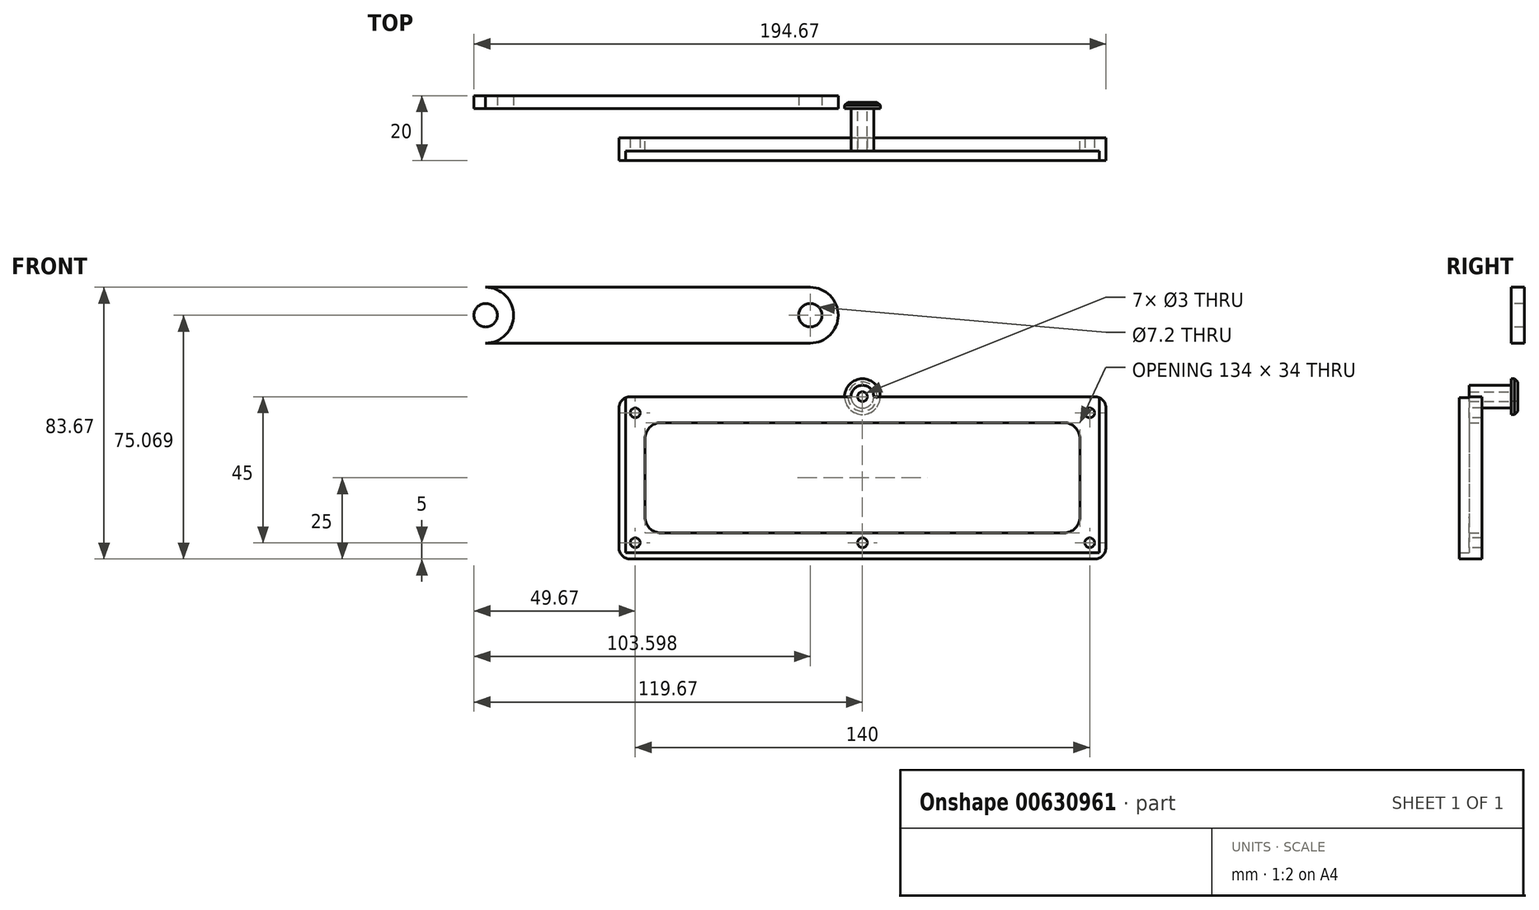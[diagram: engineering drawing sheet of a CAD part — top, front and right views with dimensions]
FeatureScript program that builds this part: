
annotation { "Feature Type Name" : "Feature", "Feature Type Description" : "" }
export const myFeature = defineFeature(function(context is Context, id is Id, definition is map)
    precondition{}
    {
        {
            var Q0;
            Q0=qCreatedBy(makeId("Front.planeOp"),FACE);
            var sketch = newSketch(context, id + "F0", { "sketchPlane" : qUnion([Q0])});
            skLineSegment(sketch, "E0.bottom", {"start": v(75, 25) * mm, "end": v(-75, 25) * mm});
            skLineSegment(sketch, "E0.top", {"start": v(75, -25) * mm, "end": v(-75, -25) * mm});
            skLineSegment(sketch, "E0.left", {"start": v(75, 25) * mm, "end": v(75, -25) * mm});
            skLineSegment(sketch, "E0.right", {"start": v(-75, 25) * mm, "end": v(-75, -25) * mm});
            skPoint(sketch, "E0.middle", {"position": v(0, 0) * mm});
            skLineSegment(sketch, "E1.bottom", {"start": v(-67, 17) * mm, "end": v(67, 17) * mm});
            skLineSegment(sketch, "E1.top", {"start": v(-67, -17) * mm, "end": v(67, -17) * mm});
            skLineSegment(sketch, "E1.left", {"start": v(-67, 17) * mm, "end": v(-67, -17) * mm});
            skLineSegment(sketch, "E1.right", {"start": v(67, 17) * mm, "end": v(67, -17) * mm});
            skLineSegment(sketch, "E2", {"start": v(0, 17) * mm, "end": v(0, 25) * mm, "construction": true});
            skArc(sketch, "E3", {"start": v(-6.5, 25) * mm, "mid": v(0, 31.5) * mm, "end": v(6.5, 25) * mm});
            skCircle(sketch, "E4", {"center": v(0, 25) * mm, "radius": 1.5 * mm});
            skLineSegment(sketch, "E5.bottom", {"start": v(7.5, 17) * mm, "end": v(-7.5, 17) * mm});
            skLineSegment(sketch, "E5.top", {"start": v(7.5, -17) * mm, "end": v(-7.5, -17) * mm});
            skLineSegment(sketch, "E5.left", {"start": v(7.5, 17) * mm, "end": v(7.5, -17) * mm});
            skLineSegment(sketch, "E5.right", {"start": v(-7.5, 17) * mm, "end": v(-7.5, -17) * mm});
            skCircle(sketch, "E6", {"center": v(0, 25) * mm, "radius": 3.5 * mm});
            skSolve(sketch);
        }
        {
            var Q0;
            Q0=makeQuery(id+"F0.imprint","IMPRINT",FACE,{"disambiguationData":[TD([[makeQuery(id+"F0.imprint","IMPRINT",EDGE,{"derivedFrom":sQuery(id+"F0.wireOp",EDGE,"E0.top")}),-1.0]])]});
            var Q1;
            {var subQ0=sQuery(id+"F0.wireOp",EDGE,"E3");Q1=makeQuery(id+"F0.imprint","IMPRINT",FACE,{"disambiguationData":[TD([[makeQuery(id+"F0.imprint","IMPRINT",EDGE,{"derivedFrom":subQ0}),-1.0]])]});}
            var Q2;
            Q2=makeQuery(id+"F0.imprint","IMPRINT",FACE,{"disambiguationData":[TD([[makeQuery(id+"F0.imprint","IMPRINT",EDGE,{"derivedFrom":sQuery(id+"F0.wireOp",EDGE,"E5.bottom")}),1.0]])]});
            var Q3;
            {var subQ0=sQuery(id+"F0.wireOp",EDGE,"E6");var subQ1=sQuery(id+"F0.wireOp",EDGE,"E0.bottom");var subQ2=makeQuery(id+"F0.imprint","INTERSECT",VERTEX,{"disambiguationData":[OD(0.0)],"derivedFrom":[subQ1,subQ0]});Q3=makeQuery(id+"F0.imprint","IMPRINT",FACE,{"disambiguationData":[TD([[makeQuery(id+"F0.imprint","IMPRINT",EDGE,{"disambiguationData":[TD([[subQ2,-1.0]])],"derivedFrom":subQ1}),1.0]])]});}
            var Q4;
            {var subQ0=sQuery(id+"F0.wireOp",EDGE,"E6");var subQ1=sQuery(id+"F0.wireOp",EDGE,"E0.bottom");var subQ2=makeQuery(id+"F0.imprint","INTERSECT",VERTEX,{"disambiguationData":[OD(0.0)],"derivedFrom":[subQ1,subQ0]});Q4=makeQuery(id+"F0.imprint","IMPRINT",FACE,{"disambiguationData":[TD([[makeQuery(id+"F0.imprint","IMPRINT",EDGE,{"disambiguationData":[TD([[subQ2,-1.0]])],"derivedFrom":subQ1}),-1.0]])]});}
            extrude(context, id + "F1", {"entities" : qUnion([Q0, Q1, Q2, Q3, Q4]), "depth" : 4 * mm, "offsetDistance" : 25 * mm});
        }
        {
            var Q0;
            {var subQ0=sQuery(id+"F0.wireOp",EDGE,"E3");var subQ1=sQuery(id+"F0.wireOp",EDGE,"E0.bottom");Q0=makeQuery(id+"F1.opExtrude","SWEPT_EDGE",EDGE,{"disambiguationData":[OSD([subQ1,subQ0]),TDD([makeQuery(id+"F0.imprint","INTERSECT",VERTEX,{"disambiguationData":[OD(0.0)],"derivedFrom":[subQ1,subQ0]})])]});}
            var Q1;
            {var subQ0=sQuery(id+"F0.wireOp",EDGE,"E3");var subQ1=sQuery(id+"F0.wireOp",EDGE,"E0.bottom");Q1=makeQuery(id+"F1.opExtrude","SWEPT_EDGE",EDGE,{"disambiguationData":[OSD([subQ1,subQ0]),TDD([makeQuery(id+"F0.imprint","INTERSECT",VERTEX,{"disambiguationData":[OD(1.0)],"derivedFrom":[subQ1,subQ0]})])]});}
            var Q2;
            Q2=makeQuery(id+"F1.opExtrude","SWEPT_EDGE",EDGE,{"disambiguationData":[OSD([sQuery(id+"F0.wireOp",EDGE,"E1.bottom"),sQuery(id+"F0.wireOp",EDGE,"E5.bottom"),sQuery(id+"F0.wireOp",EDGE,"E5.right")])]});
            var Q3;
            Q3=makeQuery(id+"F1.opExtrude","SWEPT_EDGE",EDGE,{"disambiguationData":[OSD([sQuery(id+"F0.wireOp",EDGE,"E1.bottom"),sQuery(id+"F0.wireOp",EDGE,"E5.bottom"),sQuery(id+"F0.wireOp",EDGE,"E5.left")])]});
            var Q4;
            Q4=makeQuery(id+"F1.opExtrude","SWEPT_EDGE",EDGE,{"disambiguationData":[OSD([sQuery(id+"F0.wireOp",EDGE,"E1.top"),sQuery(id+"F0.wireOp",EDGE,"E5.top"),sQuery(id+"F0.wireOp",EDGE,"E5.left")])]});
            var Q5;
            Q5=makeQuery(id+"F1.opExtrude","SWEPT_EDGE",EDGE,{"disambiguationData":[OSD([sQuery(id+"F0.wireOp",EDGE,"E1.top"),sQuery(id+"F0.wireOp",EDGE,"E5.top"),sQuery(id+"F0.wireOp",EDGE,"E5.right")])]});
            fillet(context, id + "F2", {"entities" : qUnion([Q0, Q1, Q2, Q3, Q4, Q5]), "radius" : 5 * mm, "tangentPropagation" : true, "allowEdgeOverflow" : false});
        }
        {
            var Q0;
            Q0=makeQuery(id+"F1.opExtrude","CAP_FACE",FACE,{"disambiguationData":[OSD([sQuery(id+"F0.wireOp",EDGE,"E0.bottom"),sQuery(id+"F0.wireOp",EDGE,"E0.top"),sQuery(id+"F0.wireOp",EDGE,"E0.left"),sQuery(id+"F0.wireOp",EDGE,"E0.right"),sQuery(id+"F0.wireOp",EDGE,"E1.bottom"),sQuery(id+"F0.wireOp",EDGE,"E1.top"),sQuery(id+"F0.wireOp",EDGE,"E1.left"),sQuery(id+"F0.wireOp",EDGE,"E1.right"),sQuery(id+"F0.wireOp",EDGE,"E3"),sQuery(id+"F0.wireOp",EDGE,"E4")])],"isStart":false});
            var sketch = newSketch(context, id + "F3", { "sketchPlane" : qUnion([Q0])});
            skLineSegment(sketch, "E7.bottom", {"start": v(-75, -25) * mm, "end": v(75, -25) * mm});
            skLineSegment(sketch, "E7.top", {"start": v(-75, -23) * mm, "end": v(75, -23) * mm});
            skLineSegment(sketch, "E7.left", {"start": v(-75, -25) * mm, "end": v(-75, -23) * mm});
            skLineSegment(sketch, "E7.right", {"start": v(75, -25) * mm, "end": v(75, -23) * mm});
            skLineSegment(sketch, "E8.bottom", {"start": v(75, 25) * mm, "end": v(73, 25) * mm});
            skLineSegment(sketch, "E8.top", {"start": v(75, -23) * mm, "end": v(73, -23) * mm});
            skLineSegment(sketch, "E8.left", {"start": v(75, 25) * mm, "end": v(75, -23) * mm});
            skLineSegment(sketch, "E8.right", {"start": v(73, 25) * mm, "end": v(73, -23) * mm});
            skLineSegment(sketch, "E9.bottom", {"start": v(-75, 25) * mm, "end": v(-73, 25) * mm});
            skLineSegment(sketch, "E9.top", {"start": v(-75, -23) * mm, "end": v(-73, -23) * mm});
            skLineSegment(sketch, "E9.left", {"start": v(-75, 25) * mm, "end": v(-75, -23) * mm});
            skLineSegment(sketch, "E9.right", {"start": v(-73, 25) * mm, "end": v(-73, -23) * mm});
            skSolve(sketch);
        }
        {
            var Q0;
            Q0=makeQuery(id+"F3.imprint","IMPRINT",FACE,{"disambiguationData":[TD([[makeQuery(id+"F3.imprint","IMPRINT",EDGE,{"derivedFrom":sQuery(id+"F3.wireOp",EDGE,"E9.bottom")}),1.0]])]});
            var Q1;
            Q1=makeQuery(id+"F3.imprint","IMPRINT",FACE,{"disambiguationData":[TD([[makeQuery(id+"F3.imprint","IMPRINT",EDGE,{"derivedFrom":sQuery(id+"F3.wireOp",EDGE,"E7.bottom")}),-1.0]])]});
            var Q2;
            Q2=makeQuery(id+"F3.imprint","IMPRINT",FACE,{"disambiguationData":[TD([[makeQuery(id+"F3.imprint","IMPRINT",EDGE,{"derivedFrom":sQuery(id+"F3.wireOp",EDGE,"E8.bottom")}),1.0]])]});
            extrude(context, id + "F4", {"entities" : qUnion([Q0, Q1, Q2]), "operationType" : NewBodyOperationType.ADD, "depth" : 3 * mm, "offsetDistance" : 25 * mm});
        }
        {
            var Q0;
            Q0=makeQuery(id+"F1.opExtrude","CAP_FACE",FACE,{"disambiguationData":[OSD([sQuery(id+"F0.wireOp",EDGE,"E0.bottom"),sQuery(id+"F0.wireOp",EDGE,"E0.top"),sQuery(id+"F0.wireOp",EDGE,"E0.left"),sQuery(id+"F0.wireOp",EDGE,"E0.right"),sQuery(id+"F0.wireOp",EDGE,"E1.bottom"),sQuery(id+"F0.wireOp",EDGE,"E1.top"),sQuery(id+"F0.wireOp",EDGE,"E1.left"),sQuery(id+"F0.wireOp",EDGE,"E1.right"),sQuery(id+"F0.wireOp",EDGE,"E3"),sQuery(id+"F0.wireOp",EDGE,"E4")])],"isStart":false});
            var sketch = newSketch(context, id + "F5", { "sketchPlane" : qUnion([Q0])});
            skLineSegment(sketch, "E10", {"start": v(-67, -17) * mm, "end": v(-73, -23) * mm, "construction": true});
            skLineSegment(sketch, "E11.bottom", {"start": v(-73, 25) * mm, "end": v(-71, 25) * mm, "construction": true});
            skLineSegment(sketch, "E11.top", {"start": v(-73, 23) * mm, "end": v(-71, 23) * mm, "construction": true});
            skLineSegment(sketch, "E11.left", {"start": v(-73, 25) * mm, "end": v(-73, 23) * mm, "construction": true});
            skLineSegment(sketch, "E11.right", {"start": v(-71, 25) * mm, "end": v(-71, 23) * mm, "construction": true});
            skLineSegment(sketch, "E12", {"start": v(-67, 17) * mm, "end": v(-73, 23) * mm, "construction": true});
            skLineSegment(sketch, "E13.bottom", {"start": v(73, 25) * mm, "end": v(71, 25) * mm, "construction": true});
            skLineSegment(sketch, "E13.top", {"start": v(73, 23) * mm, "end": v(71, 23) * mm, "construction": true});
            skLineSegment(sketch, "E13.left", {"start": v(73, 25) * mm, "end": v(73, 23) * mm, "construction": true});
            skLineSegment(sketch, "E13.right", {"start": v(71, 25) * mm, "end": v(71, 23) * mm, "construction": true});
            skLineSegment(sketch, "E14", {"start": v(67, 17) * mm, "end": v(73, 23) * mm, "construction": true});
            skLineSegment(sketch, "E15", {"start": v(73, -23) * mm, "end": v(67, -17) * mm, "construction": true});
            skCircle(sketch, "E16", {"center": v(-70, 20) * mm, "radius": 1.5 * mm});
            skCircle(sketch, "E17", {"center": v(70, 20) * mm, "radius": 1.5 * mm});
            skCircle(sketch, "E18", {"center": v(70, -20) * mm, "radius": 1.5 * mm});
            skCircle(sketch, "E19", {"center": v(-70, -20) * mm, "radius": 1.5 * mm});
            skLineSegment(sketch, "E20", {"start": v(-70, -20) * mm, "end": v(70, -20) * mm, "construction": true});
            skCircle(sketch, "E21", {"center": v(0, -20) * mm, "radius": 1.5 * mm});
            skSolve(sketch);
        }
        {
            var Q0;
            Q0=makeQuery(id+"F5.imprint","IMPRINT",FACE,{"disambiguationData":[TD([[makeQuery(id+"F5.imprint","IMPRINT",EDGE,{"derivedFrom":sQuery(id+"F5.wireOp",EDGE,"E16")}),1.0]])]});
            var Q1;
            Q1=makeQuery(id+"F5.imprint","IMPRINT",FACE,{"disambiguationData":[TD([[makeQuery(id+"F5.imprint","IMPRINT",EDGE,{"derivedFrom":sQuery(id+"F5.wireOp",EDGE,"E19")}),1.0]])]});
            var Q2;
            Q2=makeQuery(id+"F5.imprint","IMPRINT",FACE,{"disambiguationData":[TD([[makeQuery(id+"F5.imprint","IMPRINT",EDGE,{"derivedFrom":sQuery(id+"F5.wireOp",EDGE,"E18")}),1.0]])]});
            var Q3;
            Q3=makeQuery(id+"F5.imprint","IMPRINT",FACE,{"disambiguationData":[TD([[makeQuery(id+"F5.imprint","IMPRINT",EDGE,{"derivedFrom":sQuery(id+"F5.wireOp",EDGE,"E17")}),1.0]])]});
            var Q4;
            Q4=makeQuery(id+"F5.imprint","IMPRINT",FACE,{"disambiguationData":[TD([[makeQuery(id+"F5.imprint","IMPRINT",EDGE,{"derivedFrom":sQuery(id+"F5.wireOp",EDGE,"E21")}),1.0]])]});
            extrude(context, id + "F6", {"entities" : qUnion([Q0, Q1, Q2, Q3, Q4]), "operationType" : NewBodyOperationType.REMOVE, "oppositeDirection" : true, "depth" : 4 * mm, "offsetDistance" : 25 * mm});
        }
        {
            var Q0;
            Q0=makeQuery(id+"F4.boolean.opBoolean","MERGE",EDGE,{"derivedFrom":[makeQuery(id+"F1.opExtrude","SWEPT_EDGE",EDGE,{"disambiguationData":[OSD([sQuery(id+"F0.wireOp",EDGE,"E0.bottom"),sQuery(id+"F0.wireOp",EDGE,"E0.right")])]}),makeQuery(id+"F4.opExtrude","SWEPT_EDGE",EDGE,{"disambiguationData":[OSD([sQuery(id+"F3.wireOp",EDGE,"E9.bottom"),sQuery(id+"F3.wireOp",EDGE,"E9.left")])]})]});
            var Q1;
            Q1=makeQuery(id+"F4.boolean.opBoolean","MERGE",EDGE,{"derivedFrom":[makeQuery(id+"F1.opExtrude","SWEPT_EDGE",EDGE,{"disambiguationData":[OSD([sQuery(id+"F0.wireOp",EDGE,"E0.top"),sQuery(id+"F0.wireOp",EDGE,"E0.right")])]}),makeQuery(id+"F4.opExtrude","SWEPT_EDGE",EDGE,{"disambiguationData":[OSD([sQuery(id+"F3.wireOp",EDGE,"E7.bottom"),sQuery(id+"F3.wireOp",EDGE,"E7.left")])]})]});
            var Q2;
            Q2=makeQuery(id+"F1.opExtrude","SWEPT_EDGE",EDGE,{"disambiguationData":[OSD([sQuery(id+"F0.wireOp",EDGE,"E1.top"),sQuery(id+"F0.wireOp",EDGE,"E1.right")])]});
            var Q3;
            Q3=makeQuery(id+"F4.boolean.opBoolean","MERGE",EDGE,{"derivedFrom":[makeQuery(id+"F1.opExtrude","SWEPT_EDGE",EDGE,{"disambiguationData":[OSD([sQuery(id+"F0.wireOp",EDGE,"E0.bottom"),sQuery(id+"F0.wireOp",EDGE,"E0.left")])]}),makeQuery(id+"F4.opExtrude","SWEPT_EDGE",EDGE,{"disambiguationData":[OSD([sQuery(id+"F3.wireOp",EDGE,"E8.bottom"),sQuery(id+"F3.wireOp",EDGE,"E8.left")])]})]});
            var Q4;
            Q4=makeQuery(id+"F4.boolean.opBoolean","MERGE",EDGE,{"derivedFrom":[makeQuery(id+"F1.opExtrude","SWEPT_EDGE",EDGE,{"disambiguationData":[OSD([sQuery(id+"F0.wireOp",EDGE,"E0.top"),sQuery(id+"F0.wireOp",EDGE,"E0.left")])]}),makeQuery(id+"F4.opExtrude","SWEPT_EDGE",EDGE,{"disambiguationData":[OSD([sQuery(id+"F3.wireOp",EDGE,"E7.bottom"),sQuery(id+"F3.wireOp",EDGE,"E7.right")])]})]});
            var Q5;
            Q5=makeQuery(id+"F1.opExtrude","SWEPT_EDGE",EDGE,{"disambiguationData":[OSD([sQuery(id+"F0.wireOp",EDGE,"E1.top"),sQuery(id+"F0.wireOp",EDGE,"E1.left")])]});
            var Q6;
            Q6=makeQuery(id+"F1.opExtrude","SWEPT_EDGE",EDGE,{"disambiguationData":[OSD([sQuery(id+"F0.wireOp",EDGE,"E1.bottom"),sQuery(id+"F0.wireOp",EDGE,"E1.left")])]});
            var Q7;
            Q7=makeQuery(id+"F1.opExtrude","SWEPT_EDGE",EDGE,{"disambiguationData":[OSD([sQuery(id+"F0.wireOp",EDGE,"E1.bottom"),sQuery(id+"F0.wireOp",EDGE,"E1.right")])]});
            fillet(context, id + "F7", {"entities" : qUnion([Q0, Q1, Q2, Q3, Q4, Q5, Q6, Q7]), "radius" : 3.5 * mm, "tangentPropagation" : true, "allowEdgeOverflow" : false});
        }
        {
            var Q0;
            {var subQ0=sQuery(id+"F0.wireOp",EDGE,"E6");var subQ1=sQuery(id+"F0.wireOp",EDGE,"E0.bottom");var subQ2=makeQuery(id+"F0.imprint","INTERSECT",VERTEX,{"disambiguationData":[OD(0.0)],"derivedFrom":[subQ1,subQ0]});Q0=makeQuery(id+"F0.imprint","IMPRINT",FACE,{"disambiguationData":[TD([[makeQuery(id+"F0.imprint","IMPRINT",EDGE,{"disambiguationData":[TD([[subQ2,-1.0]])],"derivedFrom":subQ1}),-1.0]])]});}
            var Q1;
            {var subQ0=sQuery(id+"F0.wireOp",EDGE,"E6");var subQ1=sQuery(id+"F0.wireOp",EDGE,"E0.bottom");var subQ2=makeQuery(id+"F0.imprint","INTERSECT",VERTEX,{"disambiguationData":[OD(0.0)],"derivedFrom":[subQ1,subQ0]});Q1=makeQuery(id+"F0.imprint","IMPRINT",FACE,{"disambiguationData":[TD([[makeQuery(id+"F0.imprint","IMPRINT",EDGE,{"disambiguationData":[TD([[subQ2,-1.0]])],"derivedFrom":subQ1}),1.0]])]});}
            extrude(context, id + "F8", {"entities" : qUnion([Q0, Q1]), "operationType" : NewBodyOperationType.ADD, "oppositeDirection" : true, "depth" : 9 * mm, "offsetDistance" : 25 * mm});
        }
        {
            var Q0;
            Q0=makeQuery(id+"F8.opExtrude","CAP_FACE",FACE,{"disambiguationData":[OSD([sQuery(id+"F0.wireOp",EDGE,"E4"),sQuery(id+"F0.wireOp",EDGE,"E6")])],"isStart":false});
            var sketch = newSketch(context, id + "F9", { "sketchPlane" : qUnion([Q0])});
            skCircle(sketch, "E22", {"center": v(0, 25) * mm, "radius": 1.5 * mm});
            skCircle(sketch, "E23", {"center": v(0, 25) * mm, "radius": 5.5 * mm});
            skCircle(sketch, "E24", {"center": v(16.07, 50.07) * mm, "radius": 3.6 * mm});
            skCircle(sketch, "E25", {"center": v(16.07, 50.07) * mm, "radius": 8.6 * mm});
            skCircle(sketch, "E26", {"center": v(16.07, 50.07) * mm, "radius": 3.5 * mm, "construction": true});
            skLineSegment(sketch, "E27", {"start": v(16.07, 50.07) * mm, "end": v(16.07, 41.47) * mm, "construction": true});
            skLineSegment(sketch, "E28", {"start": v(16.07, 50.07) * mm, "end": v(16.07, 58.67) * mm, "construction": true});
            skLineSegment(sketch, "E29.bottom", {"start": v(66.07, 58.67) * mm, "end": v(16.07, 58.67) * mm});
            skLineSegment(sketch, "E29.top", {"start": v(66.07, 41.47) * mm, "end": v(16.07, 41.47) * mm});
            skLineSegment(sketch, "E29.left", {"start": v(66.07, 58.67) * mm, "end": v(66.07, 41.47) * mm, "construction": true});
            skLineSegment(sketch, "E29.right", {"start": v(16.07, 58.67) * mm, "end": v(16.07, 41.47) * mm});
            skLineSegment(sketch, "E30.MirrorCS", {"start": v(66.07, 58.67) * mm, "end": v(116.07, 58.67) * mm});
            skLineSegment(sketch, "E31.MirrorCS", {"start": v(66.07, 41.47) * mm, "end": v(116.07, 41.47) * mm});
            skCircle(sketch, "E32.MirrorC", {"center": v(116.07, 50.07) * mm, "radius": 8.6 * mm});
            skCircle(sketch, "E33.MirrorC", {"center": v(116.07, 50.07) * mm, "radius": 3.6 * mm});
            skSolve(sketch);
        }
        {
            var Q0;
            Q0=makeQuery(id+"F9.imprint","IMPRINT",FACE,{"disambiguationData":[TD([[makeQuery(id+"F9.imprint","IMPRINT",EDGE,{"derivedFrom":sQuery(id+"F9.wireOp",EDGE,"E22")}),1.0]])]});
            var Q1;
            Q1=makeQuery(id+"F9.imprint","IMPRINT",FACE,{"disambiguationData":[TD([[makeQuery(id+"F9.imprint","IMPRINT",EDGE,{"derivedFrom":sQuery(id+"F9.wireOp",EDGE,"E23")}),1.0]])]});
            extrude(context, id + "F10", {"entities" : qUnion([Q0, Q1]), "depth" : 2 * mm, "offsetDistance" : 25 * mm});
        }
        {
            var Q0;
            Q0=makeQuery(id+"F10.opExtrude","CAP_EDGE",EDGE,{"disambiguationData":[OSD([sQuery(id+"F9.wireOp",EDGE,"E23")])],"isStart":false});
            chamfer(context, id + "F11", {"entities" : qUnion([Q0]), "width" : 1 * mm, "tangentPropagation" : true});
        }
        {
            var Q0;
            {var subQ2=sQuery(id+"F9.wireOp",EDGE,"E29.bottom");Q0=makeQuery(id+"F9.imprint","IMPRINT",FACE,{"disambiguationData":[TD([[makeQuery(id+"F9.imprint","IMPRINT",EDGE,{"derivedFrom":subQ2}),1.0]])]});}
            var Q1;
            {var subQ0=sQuery(id+"F9.wireOp",EDGE,"E29.right");var subQ1=sQuery(id+"F9.wireOp",EDGE,"E24");var subQ2=makeQuery(id+"F9.imprint","INTERSECT",VERTEX,{"disambiguationData":[OD(0.0)],"derivedFrom":[subQ1,subQ0]});Q1=makeQuery(id+"F9.imprint","IMPRINT",FACE,{"disambiguationData":[TD([[makeQuery(id+"F9.imprint","IMPRINT",EDGE,{"disambiguationData":[TD([[subQ2,1.0]])],"derivedFrom":subQ1}),-1.0]])]});}
            var Q2;
            {var subQ0=sQuery(id+"F9.wireOp",EDGE,"E29.right");var subQ1=sQuery(id+"F9.wireOp",EDGE,"E24");var subQ2=makeQuery(id+"F9.imprint","INTERSECT",VERTEX,{"disambiguationData":[OD(0.0)],"derivedFrom":[subQ1,subQ0]});Q2=makeQuery(id+"F9.imprint","IMPRINT",FACE,{"disambiguationData":[TD([[makeQuery(id+"F9.imprint","IMPRINT",EDGE,{"disambiguationData":[TD([[subQ2,-1.0]])],"derivedFrom":subQ1}),-1.0]])]});}
            var Q3;
            Q3=makeQuery(id+"F9.imprint","IMPRINT",FACE,{"disambiguationData":[TD([[makeQuery(id+"F9.imprint","IMPRINT",EDGE,{"derivedFrom":sQuery(id+"F9.wireOp",EDGE,"E33.MirrorC")}),1.0]])]});
            extrude(context, id + "F12", {"entities" : qUnion([Q0, Q1, Q2, Q3]), "depth" : 4 * mm, "offsetDistance" : 25 * mm});
        }
    });
